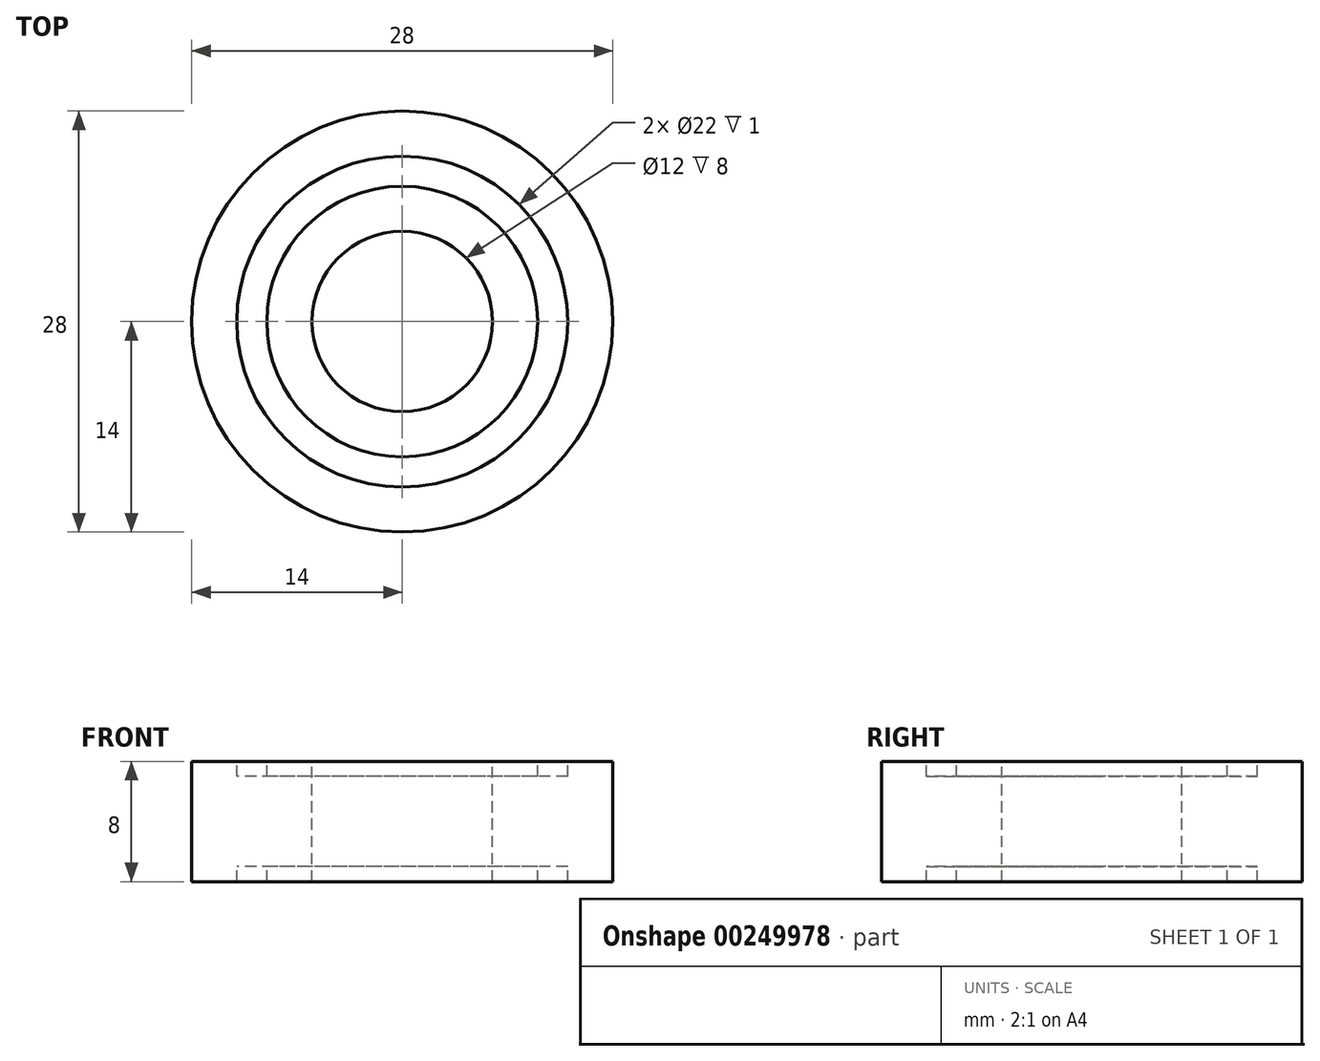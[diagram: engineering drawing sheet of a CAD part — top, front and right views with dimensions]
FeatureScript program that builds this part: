
annotation { "Feature Type Name" : "Feature", "Feature Type Description" : "" }
export const myFeature = defineFeature(function(context is Context, id is Id, definition is map)
    precondition{}
    {
        {
            var Q0;
            Q0=qCreatedBy(makeId("Front.planeOp"),FACE);
            var sketch = newSketch(context, id + "F0", { "sketchPlane" : qUnion([Q0])});
            skLineSegment(sketch, "E0", {"start": v(-14, 4) * mm, "end": v(-14, 0) * mm});
            skLineSegment(sketch, "E1", {"start": v(-14, 4) * mm, "end": v(-11, 4) * mm});
            skLineSegment(sketch, "E2", {"start": v(-6, 4) * mm, "end": v(-6, 0) * mm});
            skLineSegment(sketch, "E3", {"start": v(-11, 4) * mm, "end": v(-11, 3) * mm});
            skLineSegment(sketch, "E4", {"start": v(-9, 4) * mm, "end": v(-9, 3) * mm});
            skLineSegment(sketch, "E5", {"start": v(-11, 3) * mm, "end": v(-9, 3) * mm});
            skLineSegment(sketch, "E6.trimOffspring", {"start": v(-9, 4) * mm, "end": v(-6, 4) * mm});
            skPoint(sketch, "E7", {"position": v(0, 0) * mm});
            skLineSegment(sketch, "E8", {"start": v(0, 16.42) * mm, "end": v(0, -13.94) * mm});
            skLineSegment(sketch, "E9", {"start": v(-19, 0) * mm, "end": v(2.48, 0) * mm, "construction": true});
            skLineSegment(sketch, "E10.MirrorCS", {"start": v(-11, -4) * mm, "end": v(-11, -3) * mm});
            skLineSegment(sketch, "E11.MirrorCS", {"start": v(-9, -4) * mm, "end": v(-9, -3) * mm});
            skLineSegment(sketch, "E12.MirrorCS", {"start": v(-9, -4) * mm, "end": v(-6, -4) * mm});
            skLineSegment(sketch, "E13.MirrorCS", {"start": v(-14, -4) * mm, "end": v(-11, -4) * mm});
            skLineSegment(sketch, "E14.MirrorCS", {"start": v(-14, -4) * mm, "end": v(-14, 0) * mm});
            skLineSegment(sketch, "E15.MirrorCS", {"start": v(-11, -3) * mm, "end": v(-9, -3) * mm});
            skLineSegment(sketch, "E16.MirrorCS", {"start": v(-6, -4) * mm, "end": v(-6, 0) * mm});
            skSolve(sketch);
        }
        {
            var Q0;
            Q0=qSketchRegion(id+"F0",true);
            var Q1;
            Q1=sQuery(id+"F0.wireOp",EDGE,"E8");
            revolve(context, id + "F1", {"entities" : qUnion([Q0]), "axis" : qUnion([Q1]), "revolveType" : RevolveType.FULL});
        }
    });
